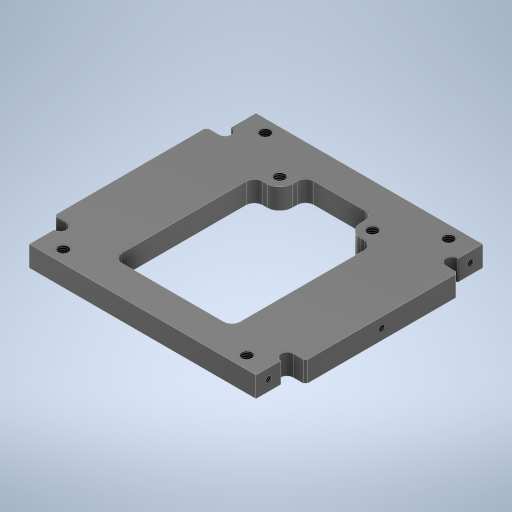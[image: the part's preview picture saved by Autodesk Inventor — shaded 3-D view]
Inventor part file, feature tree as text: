
AUTODESK INVENTOR PART (.ipt)
format: ipt  version: 2024.2 (Build 282272000, 272)  size: 371,712 bytes
history: native  units: mm
features: sketch x3, hole x2, extrude x1, chamfer x1, mirror x1
ambient origin geometry x8: Origin, YZ Plane, XZ Plane, XY Plane, X Axis, Y Axis, Z Axis, Center Point
bodies: Solid1 (feature_tree)
feature tree (8):
  sketch  "Sketch1"  dims[d0=55.0mm d1=55.0mm]
  extrude  "Extrusion1"  Depth=55.0mm
  chamfer  "C0.5"  Distance=34.0mm
  sketch  "Sketch3"  dims[d3=28.3mm d4=34.0mm d5=22.5mm d8=1.5mm d9=6.0mm d10=6.0mm d11=3.0mm d12=5.0mm d13=0.0mm d14=2.459mm d15=6.0mm d16=4.0mm d17=2.0mm d18=90.0deg d19=8.0mm d20=20.594885mm d21=1.567mm d22=4.0mm d23=4.0mm d24=2.0mm d25=90.0deg d26=6.0mm d27=0.0mm d28=0.5mm d29=2.0mm d30=45.0deg d35=6.0mm d36=0.25mm d37=0.25mm d38=2.0mm d39=6.0mm d40=8.5mm d41=16.0mm d42=1.0mm d43=3.0mm d44=3.75mm d45=49.0mm d46=1.567mm d47=4.0mm d48=5.0mm d49=3.5mm d50=90.0deg d51=6.0mm d52=0.0mm]
  hole  "Side-M2-6(1)"  [1 undecoded]
  hole  "Side-M2-6(2)"  [1 undecoded]
  mirror  "Mirror1"
  sketch  "Sketch2"  dims[d2=40.0mm]
note: 2 required parameter values undecoded (feature->parameter linkage not recoverable at this tier; creation-order binding heuristic only, values carry confidence <= 0.55)
